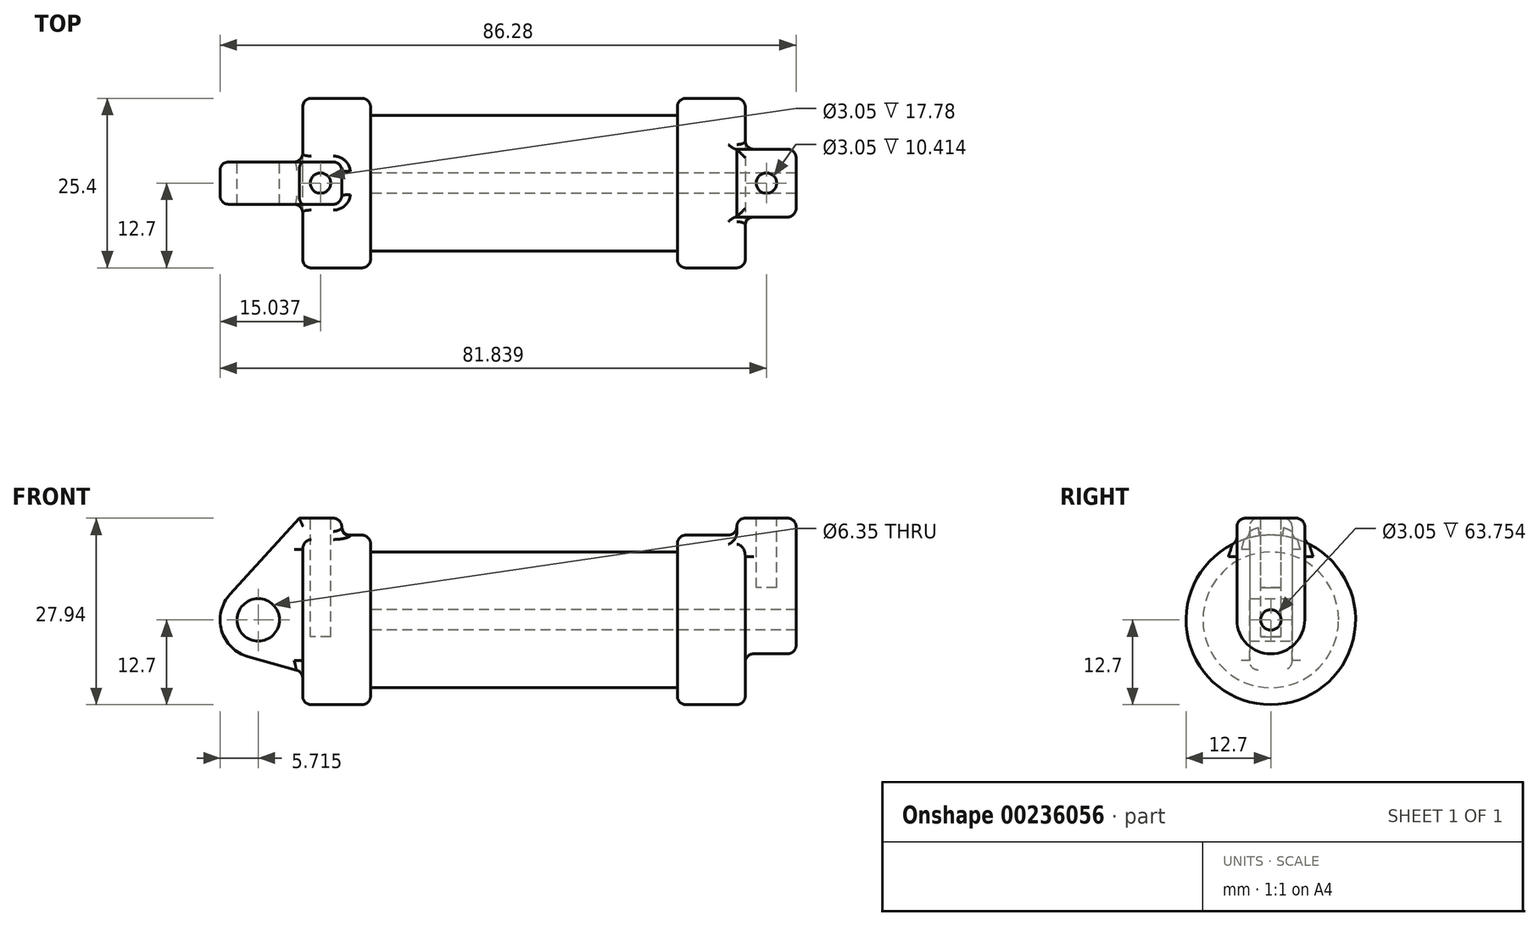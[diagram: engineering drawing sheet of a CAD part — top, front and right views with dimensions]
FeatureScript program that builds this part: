
annotation { "Feature Type Name" : "Feature", "Feature Type Description" : "" }
export const myFeature = defineFeature(function(context is Context, id is Id, definition is map)
    precondition{}
    {
        {
            var Q0;
            Q0=qCreatedBy(makeId("Front.planeOp"),FACE);
            var sketch = newSketch(context, id + "F0", { "sketchPlane" : qUnion([Q0])});
            skLineSegment(sketch, "E0", {"start": v(0, 0) * mm, "end": v(0, 12.7) * mm});
            skLineSegment(sketch, "E1", {"start": v(0, 12.7) * mm, "end": v(10.16, 12.7) * mm});
            skLineSegment(sketch, "E2", {"start": v(10.16, 12.7) * mm, "end": v(10.16, 10.16) * mm});
            skLineSegment(sketch, "E3", {"start": v(10.16, 10.16) * mm, "end": v(56.13, 10.16) * mm});
            skLineSegment(sketch, "E4", {"start": v(56.13, 10.16) * mm, "end": v(56.13, 12.7) * mm});
            skLineSegment(sketch, "E5", {"start": v(56.13, 12.7) * mm, "end": v(66.3, 12.7) * mm});
            skLineSegment(sketch, "E6", {"start": v(66.3, 12.7) * mm, "end": v(66.3, 0) * mm});
            skLineSegment(sketch, "E7", {"start": v(66.3, 0) * mm, "end": v(0, 0) * mm});
            skLineSegment(sketch, "E8", {"start": v(5.84, 15.24) * mm, "end": v(-0.5, 15.24) * mm});
            skLineSegment(sketch, "E9", {"start": v(-0.5, 15.24) * mm, "end": v(-10.88, 3.85) * mm});
            skLineSegment(sketch, "E10", {"start": v(0, 0) * mm, "end": v(-6.65, 0) * mm});
            skCircle(sketch, "E11", {"center": v(-6.65, 0) * mm, "radius": 5.72 * mm});
            skCircle(sketch, "E12", {"center": v(-6.65, 0) * mm, "radius": 3.18 * mm});
            skLineSegment(sketch, "E13", {"start": v(5.84, 15.24) * mm, "end": v(5.84, -9.4) * mm});
            skLineSegment(sketch, "E14", {"start": v(5.84, -9.4) * mm, "end": v(-8.18, -5.5) * mm});
            skSolve(sketch);
        }
        {
            var Q0;
            {var subQ0=sQuery(id+"F0.wireOp",EDGE,"E2");Q0=makeQuery(id+"F0.imprint","IMPRINT",FACE,{"disambiguationData":[TD([[makeQuery(id+"F0.imprint","IMPRINT",EDGE,{"derivedFrom":subQ0}),-1.0]])]});}
            var Q1;
            {var subQ0=sQuery(id+"F0.wireOp",EDGE,"E0");Q1=makeQuery(id+"F0.imprint","IMPRINT",FACE,{"disambiguationData":[TD([[makeQuery(id+"F0.imprint","IMPRINT",EDGE,{"derivedFrom":subQ0}),-1.0]])]});}
            var Q2;
            Q2=sQuery(id+"F0.wireOp",EDGE,"E7");
            revolve(context, id + "F1", {"entities" : qUnion([Q0, Q1]), "axis" : qUnion([Q2]), "revolveType" : RevolveType.FULL});
        }
        {
            var Q0;
            {var subQ3=sQuery(id+"F0.wireOp",EDGE,"E0");Q0=makeQuery(id+"F0.imprint","IMPRINT",FACE,{"disambiguationData":[TD([[makeQuery(id+"F0.imprint","IMPRINT",EDGE,{"derivedFrom":subQ3}),1.0]])]});}
            var Q1;
            {var subQ0=sQuery(id+"F0.wireOp",EDGE,"E0");Q1=makeQuery(id+"F0.imprint","IMPRINT",FACE,{"disambiguationData":[TD([[makeQuery(id+"F0.imprint","IMPRINT",EDGE,{"derivedFrom":subQ0}),-1.0]])]});}
            var Q2;
            {var subQ0=sQuery(id+"F0.wireOp",EDGE,"E14");Q2=makeQuery(id+"F0.imprint","IMPRINT",FACE,{"disambiguationData":[TD([[makeQuery(id+"F0.imprint","IMPRINT",EDGE,{"derivedFrom":subQ0}),-1.0]])]});}
            var Q3;
            {var subQ4=sQuery(id+"F0.wireOp",EDGE,"E12");Q3=makeQuery(id+"F0.imprint","IMPRINT",FACE,{"disambiguationData":[TD([[makeQuery(id+"F0.imprint","IMPRINT",EDGE,{"derivedFrom":subQ4}),-1.0]])]});}
            extrude(context, id + "F2", {"entities" : qUnion([Q0, Q1, Q2, Q3]), "operationType" : NewBodyOperationType.ADD, "endBound" : BoundingType.SYMMETRIC, "depth" : 6.35 * mm});
        }
        {
            var Q0;
            Q0=makeQuery(id+"F1.opRevolve","SWEPT_FACE",FACE,{"disambiguationData":[OSD([sQuery(id+"F0.wireOp",EDGE,"E6")])]});
            var sketch = newSketch(context, id + "F3", { "sketchPlane" : qUnion([Q0])});
            skCircle(sketch, "E15", {"center": v(0, 0) * mm, "radius": 1.52 * mm});
            skCircle(sketch, "E16", {"center": v(0, 0) * mm, "radius": 5.08 * mm});
            skLineSegment(sketch, "E17", {"start": v(5.08, 0) * mm, "end": v(5.08, 15.24) * mm});
            skLineSegment(sketch, "E18", {"start": v(-5.08, 0) * mm, "end": v(-5.08, 15.24) * mm});
            skLineSegment(sketch, "E19", {"start": v(-5.08, 15.24) * mm, "end": v(5.08, 15.24) * mm});
            skSolve(sketch);
        }
        {
            var Q0;
            Q0=makeQuery(id+"F3.imprint","IMPRINT",FACE,{"disambiguationData":[TD([[makeQuery(id+"F3.imprint","IMPRINT",EDGE,{"derivedFrom":sQuery(id+"F3.wireOp",EDGE,"E15")}),-1.0]])]});
            var Q1;
            {var subQ0=sQuery(id+"F3.wireOp",EDGE,"E19");Q1=makeQuery(id+"F3.imprint","IMPRINT",FACE,{"disambiguationData":[TD([[makeQuery(id+"F3.imprint","IMPRINT",EDGE,{"derivedFrom":subQ0}),-1.0]])]});}
            var Q2;
            {var subQ0=sQuery(id+"F3.wireOp",EDGE,"E17");var subQ1=sQuery(id+"F3.wireOp",EDGE,"E16");var subQ2=makeQuery(id+"F3.imprint","INTERSECT",VERTEX,{"derivedFrom":[subQ1,subQ0]});Q2=makeQuery(id+"F3.imprint","IMPRINT",FACE,{"disambiguationData":[TD([[makeQuery(id+"F3.imprint","IMPRINT",EDGE,{"disambiguationData":[TD([[subQ2,-1.0]])],"derivedFrom":subQ1}),-1.0]])]});}
            extrude(context, id + "F4", {"entities" : qUnion([Q0, Q1, Q2]), "operationType" : NewBodyOperationType.ADD, "depth" : 7.62 * mm, "hasSecondDirection" : true, "secondDirectionOppositeDirection" : true, "secondDirectionDepth" : 1.27 * mm});
        }
        {
            var Q0;
            Q0=makeQuery(id+"F2.opExtrude","SWEPT_FACE",FACE,{"disambiguationData":[OSD([sQuery(id+"F0.wireOp",EDGE,"E8")])]});
            var sketch = newSketch(context, id + "F5", { "sketchPlane" : qUnion([Q0])});
            skCircle(sketch, "E20", {"center": v(2.67, 0) * mm, "radius": 1.52 * mm});
            skSolve(sketch);
        }
        {
            var Q0;
            Q0=makeQuery(id+"F4.opExtrude","SWEPT_FACE",FACE,{"disambiguationData":[OSD([sQuery(id+"F3.wireOp",EDGE,"E19")])]});
            var sketch = newSketch(context, id + "F6", { "sketchPlane" : qUnion([Q0])});
            skCircle(sketch, "E21", {"center": v(69.47, 0) * mm, "radius": 1.52 * mm});
            skSolve(sketch);
        }
        {
            var Q0;
            Q0 = qSketchRegion(id + "F5", true);
            extrude(context, id + "F7", {"entities" : qUnion([Q0]), "operationType" : NewBodyOperationType.REMOVE, "oppositeDirection" : true, "depth" : 17.78 * mm});
        }
        {
            var Q0;
            Q0 = qSketchRegion(id + "F6", true);
            extrude(context, id + "F8", {"entities" : qUnion([Q0]), "operationType" : NewBodyOperationType.REMOVE, "oppositeDirection" : true, "depth" : 10.4 * mm});
        }
        {
            var Q0;
            Q0=makeQuery(id+"F2.opExtrude","CAP_EDGE",EDGE,{"disambiguationData":[OSD([sQuery(id+"F0.wireOp",EDGE,"E8")])],"isStart":false});
            var Q1;
            Q1=makeQuery(id+"F2.opExtrude","CAP_EDGE",EDGE,{"disambiguationData":[OSD([sQuery(id+"F0.wireOp",EDGE,"E9")])],"isStart":false});
            var Q2;
            Q2=makeQuery(id+"F1.opRevolve","SWEPT_EDGE",EDGE,{"disambiguationData":[OSD([sQuery(id+"F0.wireOp",EDGE,"E0"),sQuery(id+"F0.wireOp",EDGE,"E1")])]});
            var Q3;
            Q3=makeQuery(id+"F1.opRevolve","SWEPT_EDGE",EDGE,{"disambiguationData":[OSD([sQuery(id+"F0.wireOp",EDGE,"E1"),sQuery(id+"F0.wireOp",EDGE,"E2")])]});
            var Q4;
            Q4=makeQuery(id+"F1.opRevolve","SWEPT_EDGE",EDGE,{"disambiguationData":[OSD([sQuery(id+"F0.wireOp",EDGE,"E4"),sQuery(id+"F0.wireOp",EDGE,"E5")])]});
            var Q5;
            Q5=makeQuery(id+"F1.opRevolve","SWEPT_EDGE",EDGE,{"disambiguationData":[OSD([sQuery(id+"F0.wireOp",EDGE,"E5"),sQuery(id+"F0.wireOp",EDGE,"E6")])]});
            var Q6;
            Q6=makeQuery(id+"F4.opExtrude","SWEPT_EDGE",EDGE,{"disambiguationData":[OSD([sQuery(id+"F3.wireOp",EDGE,"E18"),sQuery(id+"F3.wireOp",EDGE,"E19")])]});
            var Q7;
            Q7=makeQuery(id+"F4.opExtrude","CAP_EDGE",EDGE,{"disambiguationData":[OSD([sQuery(id+"F3.wireOp",EDGE,"E19")])],"isStart":false});
            var Q8;
            Q8=makeQuery(id+"F4.opExtrude","CAP_EDGE",EDGE,{"disambiguationData":[OSD([sQuery(id+"F3.wireOp",EDGE,"E17")])],"isStart":false});
            var Q9;
            Q9=makeQuery(id+"F4.opExtrude","CAP_EDGE",EDGE,{"disambiguationData":[OSD([sQuery(id+"F3.wireOp",EDGE,"E19")])],"isStart":true});
            var Q10;
            Q10=makeQuery(id+"F4.opExtrude","SWEPT_EDGE",EDGE,{"disambiguationData":[OSD([sQuery(id+"F3.wireOp",EDGE,"E17"),sQuery(id+"F3.wireOp",EDGE,"E19")])]});
            var Q11;
            Q11=makeQuery(id+"F4.opExtrude","CAP_EDGE",EDGE,{"disambiguationData":[OSD([sQuery(id+"F3.wireOp",EDGE,"E18")])],"isStart":false});
            var Q12;
            Q12=makeQuery(id+"F2.opExtrude","CAP_EDGE",EDGE,{"disambiguationData":[OSD([sQuery(id+"F0.wireOp",EDGE,"E13")])],"isStart":false});
            var Q13;
            Q13=makeQuery(id+"F2.opExtrude","SWEPT_EDGE",EDGE,{"disambiguationData":[OSD([sQuery(id+"F0.wireOp",EDGE,"E8"),sQuery(id+"F0.wireOp",EDGE,"E13")])]});
            var Q14;
            Q14=makeQuery(id+"F2.opExtrude","CAP_EDGE",EDGE,{"disambiguationData":[OSD([sQuery(id+"F0.wireOp",EDGE,"E13")])],"isStart":true});
            var Q15;
            Q15=makeQuery(id+"F2.opExtrude","CAP_EDGE",EDGE,{"disambiguationData":[OSD([sQuery(id+"F0.wireOp",EDGE,"E8")])],"isStart":true});
            var Q16;
            Q16=makeQuery(id+"F2.opExtrude","CAP_EDGE",EDGE,{"disambiguationData":[OSD([sQuery(id+"F0.wireOp",EDGE,"E9")])],"isStart":true});
            var Q17;
            Q17=makeQuery(id+"F2.opExtrude","CAP_EDGE",EDGE,{"disambiguationData":[OSD([sQuery(id+"F0.wireOp",EDGE,"E14")])],"isStart":false});
            var Q18;
            Q18=makeQuery(id+"F2.opExtrude","CAP_EDGE",EDGE,{"disambiguationData":[OSD([sQuery(id+"F0.wireOp",EDGE,"E14")])],"isStart":true});
            fillet(context, id + "F9", {"entities" : qUnion([Q0, Q1, Q2, Q3, Q4, Q5, Q6, Q7, Q8, Q9, Q10, Q11, Q12, Q13, Q14, Q15, Q16, Q17, Q18]), "radius" : 1.27 * mm, "tangentPropagation" : true, "allowEdgeOverflow" : false});
        }
        {
            var Q0;
            Q0=makeQuery(id+"F2.boolean.opBoolean","INTERSECT",EDGE,{"derivedFrom":[makeQuery(id+"F1.opRevolve","SWEPT_FACE",FACE,{"disambiguationData":[OSD([sQuery(id+"F0.wireOp",EDGE,"E1")])]}),makeQuery(id+"F2.opExtrude","SWEPT_FACE",FACE,{"disambiguationData":[OSD([sQuery(id+"F0.wireOp",EDGE,"E13")])]})]});
            var Q1;
            Q1=makeQuery(id+"F4.boolean.opBoolean","INTERSECT",EDGE,{"derivedFrom":[makeQuery(id+"F1.opRevolve","SWEPT_FACE",FACE,{"disambiguationData":[OSD([sQuery(id+"F0.wireOp",EDGE,"E5")])]}),makeQuery(id+"F4.opExtrude","CAP_FACE",FACE,{"disambiguationData":[OSD([sQuery(id+"F3.wireOp",EDGE,"E15"),sQuery(id+"F3.wireOp",EDGE,"E16"),sQuery(id+"F3.wireOp",EDGE,"E17"),sQuery(id+"F3.wireOp",EDGE,"E18"),sQuery(id+"F3.wireOp",EDGE,"E19")])],"isStart":true})]});
            var Q2;
            Q2=makeQuery(id+"F9.opFillet","BLEND_EDGE",EDGE,{"blendedFrom":[makeQuery(id+"F1.opRevolve","SWEPT_EDGE",EDGE,{"disambiguationData":[OSD([sQuery(id+"F0.wireOp",EDGE,"E5"),sQuery(id+"F0.wireOp",EDGE,"E6")])]}),makeQuery(id+"F4.opExtrude","SWEPT_FACE",FACE,{"disambiguationData":[OSD([sQuery(id+"F3.wireOp",EDGE,"E18")])]})],"blendedInto":[makeQuery(id+"F4.opExtrude","SWEPT_FACE",FACE,{"disambiguationData":[OSD([sQuery(id+"F3.wireOp",EDGE,"E18")])]})]});
            fillet(context, id + "F10", {"entities" : qUnion([Q0, Q1, Q2]), "radius" : 1.27 * mm, "tangentPropagation" : true, "allowEdgeOverflow" : false});
        }
        {
            var Q0;
            Q0=makeQuery(id+"F4.boolean.opBoolean","SPLIT",FACE,{"disambiguationData":[TD([makeQuery(id+"F4.opExtrude","SWEPT_FACE",FACE,{"disambiguationData":[OSD([sQuery(id+"F3.wireOp",EDGE,"E15")])]})])],"derivedFrom":makeQuery(id+"F1.opRevolve","SWEPT_FACE",FACE,{"disambiguationData":[OSD([sQuery(id+"F0.wireOp",EDGE,"E6")])]})});
            var Q1;
            Q1=makeQuery(id+"F1.opRevolve","SWEPT_FACE",FACE,{"disambiguationData":[OSD([sQuery(id+"F0.wireOp",EDGE,"E2")])]});
            extrude(context, id + "F11", {"entities" : qUnion([Q0]), "operationType" : NewBodyOperationType.REMOVE, "endBound" : BoundingType.UP_TO_SURFACE, "oppositeDirection" : true, "endBoundEntityFace" : qUnion([Q1]), "depth" : 25.4 * mm});
        }
    });
